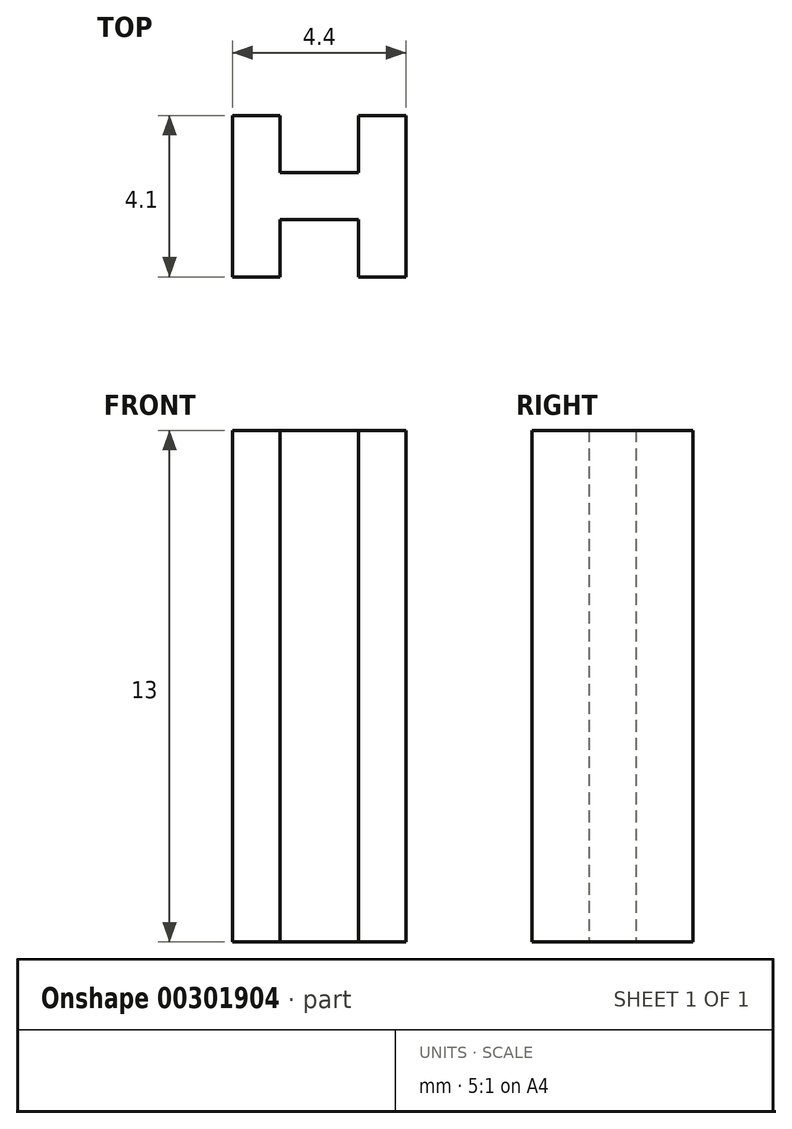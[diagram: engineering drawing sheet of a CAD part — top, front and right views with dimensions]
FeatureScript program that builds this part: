
annotation { "Feature Type Name" : "Feature", "Feature Type Description" : "" }
export const myFeature = defineFeature(function(context is Context, id is Id, definition is map)
    precondition{}
    {
        {
            var Q0;
            Q0=qCreatedBy(makeId("Top.planeOp"),FACE);
            var sketch = newSketch(context, id + "F0", { "sketchPlane" : qUnion([Q0])});
            skLineSegment(sketch, "E0", {"start": v(0, 0.6) * mm, "end": v(1, 0.6) * mm});
            skLineSegment(sketch, "E1", {"start": v(1, 0.6) * mm, "end": v(1, 2.05) * mm});
            skLineSegment(sketch, "E2", {"start": v(1, 2.05) * mm, "end": v(2.2, 2.05) * mm});
            skLineSegment(sketch, "E3", {"start": v(2.2, 2.05) * mm, "end": v(2.2, -2.05) * mm});
            skLineSegment(sketch, "E4", {"start": v(2.2, -2.05) * mm, "end": v(1, -2.05) * mm});
            skLineSegment(sketch, "E5", {"start": v(1, -2.05) * mm, "end": v(1, -0.6) * mm});
            skLineSegment(sketch, "E6", {"start": v(1, -0.6) * mm, "end": v(0, -0.6) * mm});
            skLineSegment(sketch, "E7", {"start": v(0, -0.6) * mm, "end": v(-1, -0.6) * mm});
            skLineSegment(sketch, "E8", {"start": v(-1, -0.6) * mm, "end": v(-1, -2.05) * mm});
            skLineSegment(sketch, "E9", {"start": v(-1, -2.05) * mm, "end": v(-2.2, -2.05) * mm});
            skLineSegment(sketch, "E10", {"start": v(-2.2, -2.05) * mm, "end": v(-2.2, 2.05) * mm});
            skLineSegment(sketch, "E11", {"start": v(0, 0.6) * mm, "end": v(-1, 0.6) * mm});
            skLineSegment(sketch, "E12", {"start": v(-1, 0.6) * mm, "end": v(-1, 2.05) * mm});
            skLineSegment(sketch, "E13", {"start": v(-1, 2.05) * mm, "end": v(-2.2, 2.05) * mm});
            skSolve(sketch);
        }
        {
            var Q0;
            Q0=makeQuery(id+"F0.imprint","IMPRINT",FACE,{"disambiguationData":[TD([[makeQuery(id+"F0.imprint","IMPRINT",EDGE,{"derivedFrom":sQuery(id+"F0.wireOp",EDGE,"E0")}),-1.0]])]});
            extrude(context, id + "F1", {"entities" : qUnion([Q0]), "depth" : 13 * mm});
        }
    });
